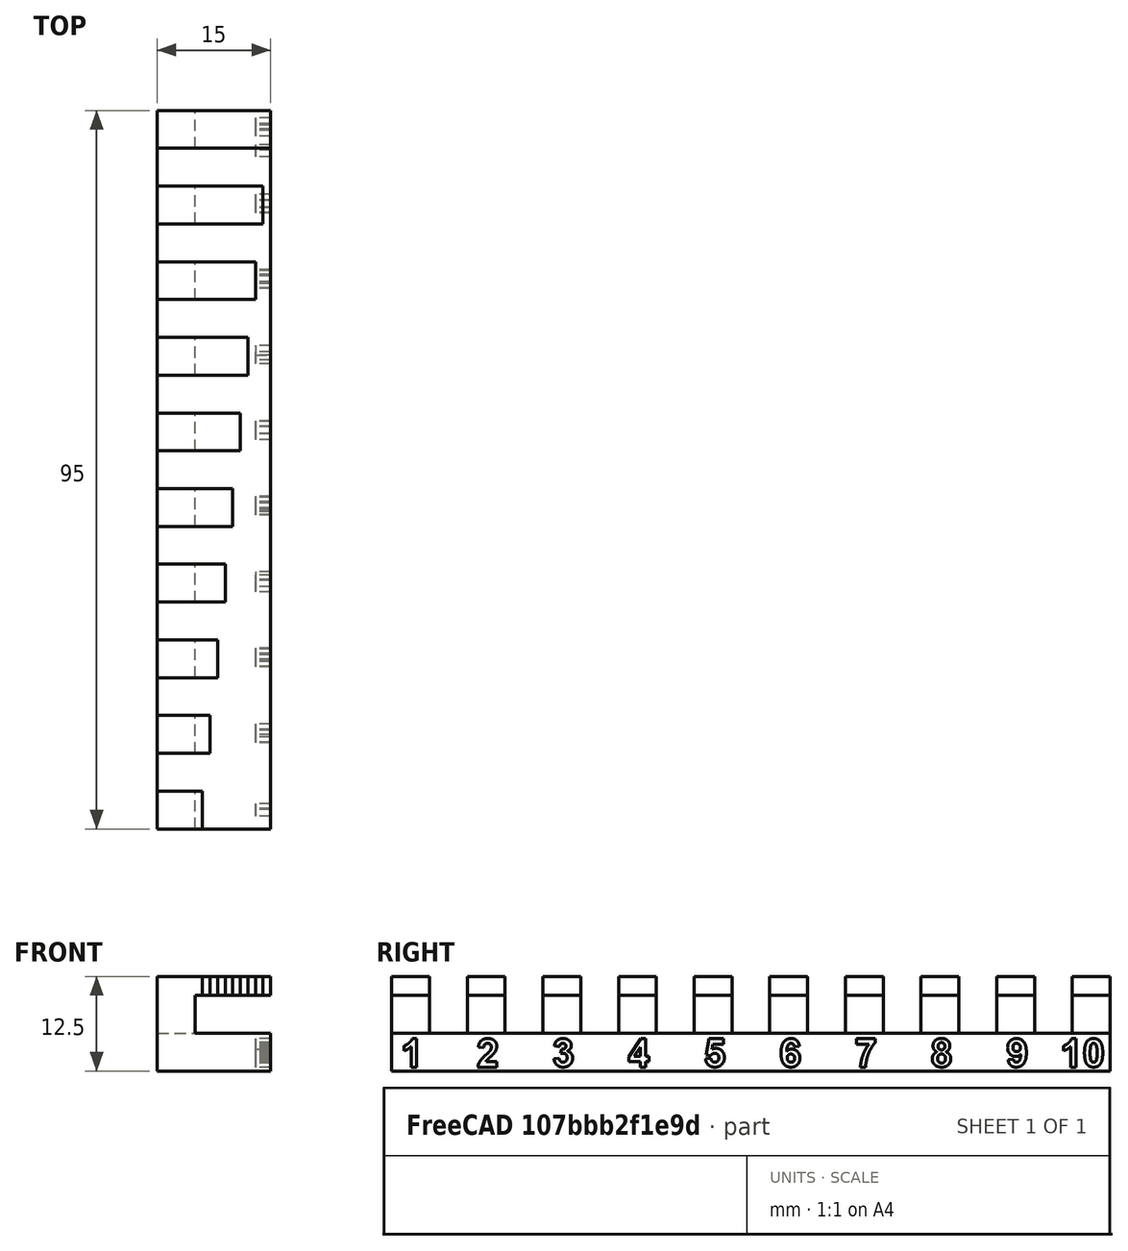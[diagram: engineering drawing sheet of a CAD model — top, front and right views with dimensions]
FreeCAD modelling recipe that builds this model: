
FCSTD DOCUMENT  (FreeCAD 0.18.3R)
Label: free
License: All rights reserved
LicenseURL: http://en.wikipedia.org/wiki/All_rights_reserved
objects: Part::Box×21, Part::MultiFuse×11, Part::Part2DObjectPython×1, Part::Extrusion×1, Part::Cut×1
note: 35 computed .brp shape members not serialized (recipe doc carries the construction recipe); baked Part::Feature solids carry a one-line shape summary decoded from their .brp

FEATURE [Part::Box] Box  label="Cube"
  AttacherType = Attacher::AttachEngine3D
  Height = 5
  Length = 5
  Width = 5
FEATURE [Part::Box] Box002  label="Cube002"
  AttacherType = Attacher::AttachEngine3D
  Height = 2.5
  Length = 6
  Placement = pos=(0,0,5) rot=(0,0,1;0rad)
  Width = 5
FEATURE [Part::MultiFuse] Fusion  label="1"
  Shapes = -> [Box002,Box]
FEATURE [Part::Box] Box003  label="Cube003"
  AttacherType = Attacher::AttachEngine3D
  Height = 2.5
  Length = 7
  Placement = pos=(0,10,5) rot=(0,0,1;0rad)
  Width = 5
FEATURE [Part::Box] Box004  label="Cube004"
  AttacherType = Attacher::AttachEngine3D
  Height = 5
  Length = 5
  Placement = pos=(0,10,0) rot=(0,0,1;0rad)
  Width = 5
FEATURE [Part::MultiFuse] Fusion001  label="2"
  Shapes = -> [Box003,Box004]
FEATURE [Part::Box] Box006  label="Cube006"
  AttacherType = Attacher::AttachEngine3D
  Height = 2.5
  Length = 8
  Placement = pos=(0,20,5) rot=(0,0,1;0rad)
  Width = 5
FEATURE [Part::Box] Box007  label="Cube007"
  AttacherType = Attacher::AttachEngine3D
  Height = 5
  Length = 5
  Placement = pos=(0,20,0) rot=(0,0,1;0rad)
  Width = 5
FEATURE [Part::MultiFuse] Fusion002  label="3"
  Shapes = -> [Box006,Box007]
FEATURE [Part::Box] Box009  label="base"
  AttacherType = Attacher::AttachEngine3D
  Height = 5
  Length = 15
  Placement = pos=(0,0,-5) rot=(0,0,1;0rad)
  Width = 95
FEATURE [Part::Box] Box010  label="Cube009"
  AttacherType = Attacher::AttachEngine3D
  Height = 2.5
  Length = 9
  Placement = pos=(0,30,5) rot=(0,0,1;0rad)
  Width = 5
FEATURE [Part::Box] Box012  label="Cube011"
  AttacherType = Attacher::AttachEngine3D
  Height = 5
  Length = 5
  Placement = pos=(0,30,0) rot=(0,0,1;0rad)
  Width = 5
FEATURE [Part::MultiFuse] Fusion004  label="4"
  Shapes = -> [Box010,Box012]
FEATURE [Part::Box] Box013  label="Cube012"
  AttacherType = Attacher::AttachEngine3D
  Height = 5
  Length = 5
  Placement = pos=(0,40,0) rot=(0,0,1;0rad)
  Width = 5
FEATURE [Part::Box] Box015  label="Cube014"
  AttacherType = Attacher::AttachEngine3D
  Height = 2.5
  Length = 10
  Placement = pos=(0,40,5) rot=(0,0,1;0rad)
  Width = 5
FEATURE [Part::MultiFuse] Fusion005  label="5"
  Shapes = -> [Box015,Box013]
FEATURE [Part::Box] Box017  label="Cube016"
  AttacherType = Attacher::AttachEngine3D
  Height = 5
  Length = 5
  Placement = pos=(0,50,0) rot=(0,0,1;0rad)
  Width = 5
FEATURE [Part::Box] Box018  label="Cube017"
  AttacherType = Attacher::AttachEngine3D
  Height = 2.5
  Length = 11
  Placement = pos=(0,50,5) rot=(0,0,1;0rad)
  Width = 5
FEATURE [Part::MultiFuse] Fusion006  label="6"
  Shapes = -> [Box018,Box017]
FEATURE [Part::Box] Box020  label="Cube019"
  AttacherType = Attacher::AttachEngine3D
  Height = 5
  Length = 5
  Placement = pos=(0,60,0) rot=(0,0,1;0rad)
  Width = 5
FEATURE [Part::Box] Box021  label="Cube020"
  AttacherType = Attacher::AttachEngine3D
  Height = 2.5
  Length = 12
  Placement = pos=(0,60,5) rot=(0,0,1;0rad)
  Width = 5
FEATURE [Part::MultiFuse] Fusion007  label="7"
  Shapes = -> [Box021,Box020]
FEATURE [Part::Box] Box023  label="Cube022"
  AttacherType = Attacher::AttachEngine3D
  Height = 2.5
  Length = 13
  Placement = pos=(0,70,5) rot=(0,0,1;0rad)
  Width = 5
FEATURE [Part::Box] Box024  label="Cube023"
  AttacherType = Attacher::AttachEngine3D
  Height = 5
  Length = 5
  Placement = pos=(0,70,0) rot=(0,0,1;0rad)
  Width = 5
FEATURE [Part::MultiFuse] Fusion008  label="8"
  Shapes = -> [Box023,Box024]
FEATURE [Part::Box] Box026  label="Cube025"
  AttacherType = Attacher::AttachEngine3D
  Height = 2.5
  Length = 14
  Placement = pos=(0,80,5) rot=(0,0,1;0rad)
  Width = 5
FEATURE [Part::Box] Box027  label="Cube026"
  AttacherType = Attacher::AttachEngine3D
  Height = 5
  Length = 5
  Placement = pos=(0,80,0) rot=(0,0,1;0rad)
  Width = 5
FEATURE [Part::MultiFuse] Fusion009  label="9"
  Shapes = -> [Box026,Box027]
FEATURE [Part::Box] Box028  label="Cube027"
  AttacherType = Attacher::AttachEngine3D
  Height = 2.5
  Length = 15
  Placement = pos=(0,90,5) rot=(0,0,1;0rad)
  Width = 5
FEATURE [Part::Box] Box030  label="Cube029"
  AttacherType = Attacher::AttachEngine3D
  Height = 5
  Length = 5
  Placement = pos=(0,90,0) rot=(0,0,1;0rad)
  Width = 5
FEATURE [Part::MultiFuse] Fusion010  label="10"
  Shapes = -> [Box028,Box030]
FEATURE [Part::MultiFuse] Fusion003  label="overhangs"
  Shapes = -> [Box009,Fusion002,Fusion001,Fusion,Fusion004,Fusion005,Fusion006,Fusion007,Fusion008,Fusion009,Fusion010]
FEATURE [Part::Part2DObjectPython] ShapeString  # Draft 2D object (typed FeaturePython)
  FontFile = <userpath>/git/aws2/bin/fonts/Arial Bold.ttf
  Placement = pos=(15,1.26,-4.5) rot=(0.57735,0.57735,0.57735;2.0944rad)
  Size = 4
  String = 1     2     3     4     5     6     7     8     9   10
  Support = -> [Fusion003]
  Tracking = 0
FEATURE [Part::Extrusion] Extrude
  Base = -> ShapeString
  Dir = (1,-1e-16,2e-16)
  DirMode = 2
  FaceMakerClass = Part::FaceMakerBullseye
  LengthFwd = -2
  LengthRev = 0
  Solid = false
  Symmetric = false
FEATURE [Part::Cut] Cut
  Base = -> Fusion003
  Tool = -> Extrude
